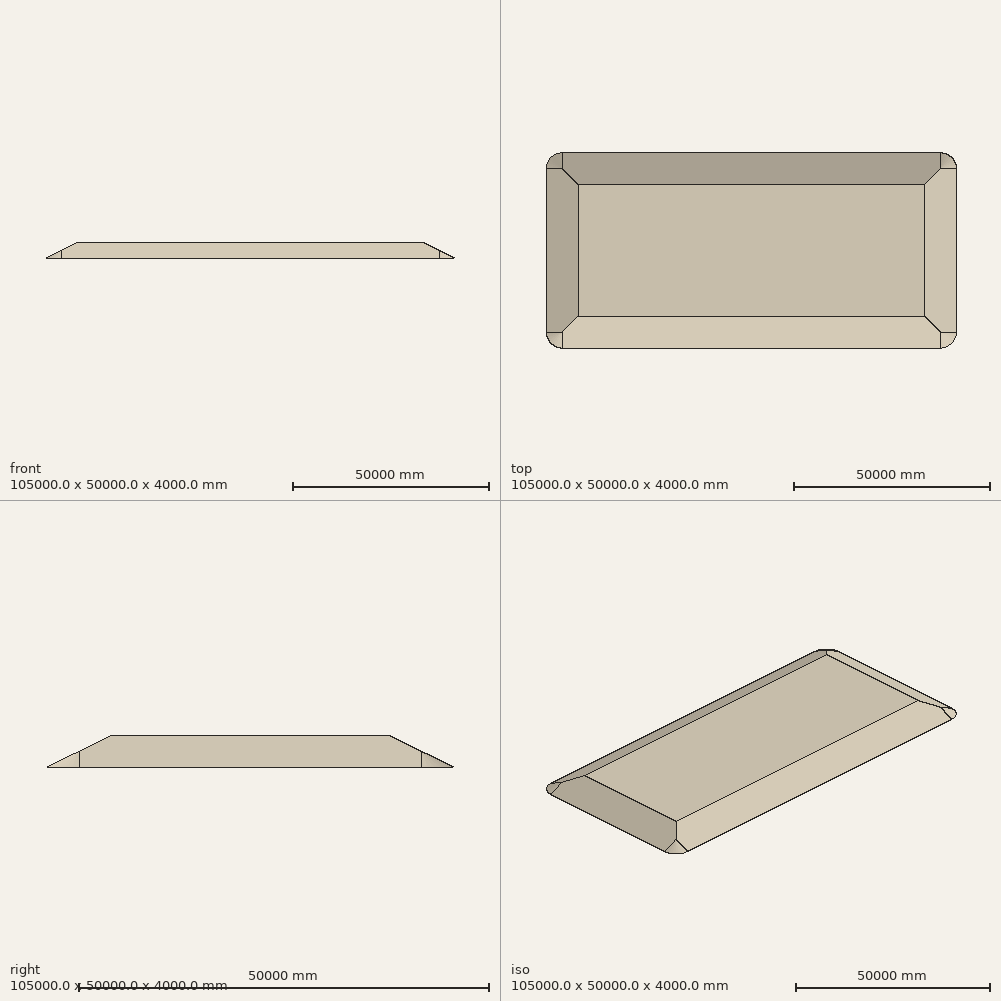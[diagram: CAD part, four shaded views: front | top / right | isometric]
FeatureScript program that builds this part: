
annotation { "Feature Type Name" : "Feature", "Feature Type Description" : "" }
export const myFeature = defineFeature(function(context is Context, id is Id, definition is map)
    precondition{}
    {
        {
            var Q0;
            Q0=qCreatedBy(makeId("Top.planeOp"),FACE);
            var sketch = newSketch(context, id + "F0", { "sketchPlane" : qUnion([Q0])});
            skLineSegment(sketch, "E0.bottom", {"start": v(-100848.3, 49955.58) * mm, "end": v(-4048.3, 49955.58) * mm});
            skLineSegment(sketch, "E0.top", {"start": v(-100848.3, -44.42) * mm, "end": v(-4048.3, -44.42) * mm});
            skLineSegment(sketch, "E0.left", {"start": v(-104948.3, 45855.58) * mm, "end": v(-104948.3, 4055.58) * mm});
            skLineSegment(sketch, "E0.right", {"start": v(51.7, 45855.58) * mm, "end": v(51.7, 4055.58) * mm});
            skPoint(sketch, "E1.visualSharp", {"position": v(-104948.3, 49955.58) * mm});
            skArc(sketch, "E1.filletArc", {"start": v(-100848.3, 49955.58) * mm, "mid": v(-103747.43, 48754.72) * mm, "end": v(-104948.3, 45855.58) * mm});
            skPoint(sketch, "E2.visualSharp", {"position": v(-104948.3, -44.42) * mm});
            skArc(sketch, "E2.filletArc", {"start": v(-104948.3, 4055.58) * mm, "mid": v(-103747.43, 1156.44) * mm, "end": v(-100848.3, -44.42) * mm});
            skPoint(sketch, "E3.visualSharp", {"position": v(51.7, -44.42) * mm});
            skArc(sketch, "E3.filletArc", {"start": v(-4048.3, -44.42) * mm, "mid": v(-1149.15, 1156.44) * mm, "end": v(51.7, 4055.58) * mm});
            skPoint(sketch, "E4.visualSharp", {"position": v(51.7, 49955.58) * mm});
            skArc(sketch, "E4.filletArc", {"start": v(51.7, 45855.58) * mm, "mid": v(-1149.15, 48754.72) * mm, "end": v(-4048.3, 49955.58) * mm});
            skSolve(sketch);
        }
        {
            var Q0;
            Q0=makeQuery(id+"F0.imprint","IMPRINT",FACE,{"disambiguationData":[TD([[makeQuery(id+"F0.imprint","IMPRINT",EDGE,{"derivedFrom":sQuery(id+"F0.wireOp",EDGE,"E0.bottom")}),-1.0]])]});
            extrude(context, id + "F1", {"entities" : qUnion([Q0]), "depth" : 4000 * mm, "hasDraft" : true, "draftAngle" : 64 * degree, "draftPullDirection" : true});
        }
    });
